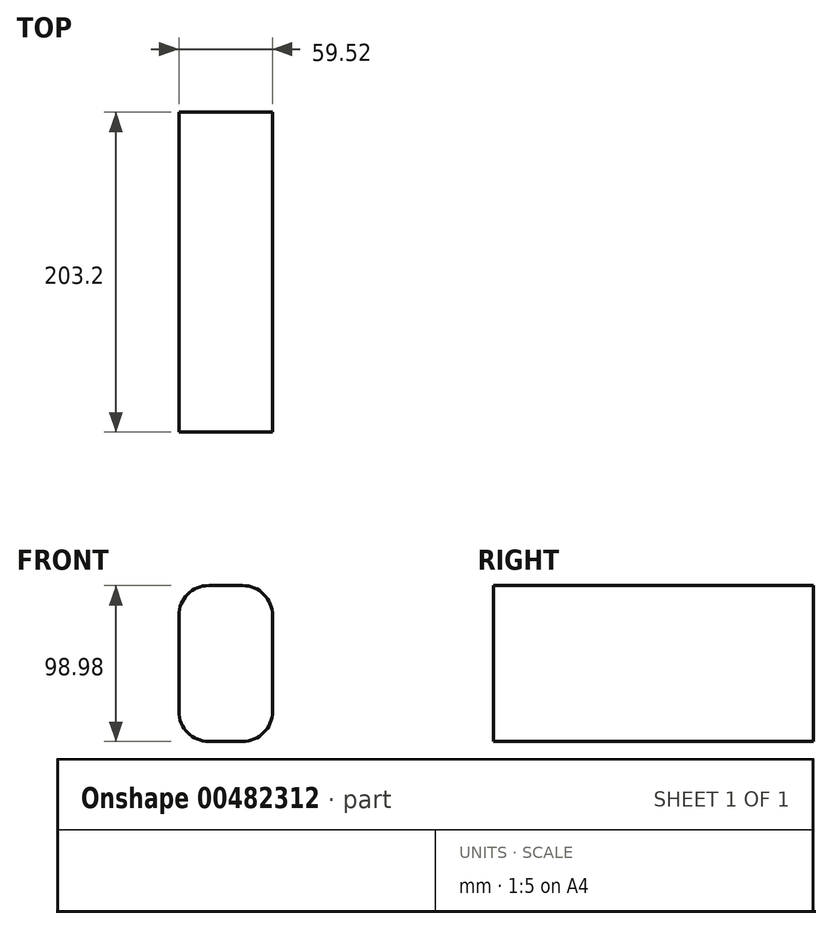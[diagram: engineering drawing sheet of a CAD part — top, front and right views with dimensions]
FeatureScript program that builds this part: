
annotation { "Feature Type Name" : "Feature", "Feature Type Description" : "" }
export const myFeature = defineFeature(function(context is Context, id is Id, definition is map)
    precondition{}
    {
        {
            var Q0;
            Q0=qCreatedBy(makeId("Front.planeOp"),FACE);
            var sketch = newSketch(context, id + "F0", { "sketchPlane" : qUnion([Q0])});
            skLineSegment(sketch, "E0.bottom", {"start": v(0, 46.05) * mm, "end": v(59.52, 46.05) * mm});
            skLineSegment(sketch, "E0.top", {"start": v(0, -52.93) * mm, "end": v(59.52, -52.93) * mm});
            skLineSegment(sketch, "E0.left", {"start": v(0, 46.05) * mm, "end": v(0, -52.93) * mm});
            skLineSegment(sketch, "E0.right", {"start": v(59.52, 46.05) * mm, "end": v(59.52, -52.93) * mm});
            skSolve(sketch);
        }
        {
            var Q0;
            Q0=makeQuery(id+"F0.imprint","IMPRINT",FACE,{"disambiguationData":[TD([[makeQuery(id+"F0.imprint","IMPRINT",EDGE,{"derivedFrom":sQuery(id+"F0.wireOp",EDGE,"E0.bottom")}),-1.0]])]});
            extrude(context, id + "F1", {"entities" : qUnion([Q0]), "depth" : 203.2 * mm, "offsetDistance" : 25.4 * mm});
        }
        {
            var Q0;
            Q0=makeQuery(id+"F1.opExtrude","SWEPT_EDGE",EDGE,{"disambiguationData":[OSD([sQuery(id+"F0.wireOp",EDGE,"E0.top"),sQuery(id+"F0.wireOp",EDGE,"E0.left")])]});
            var Q1;
            Q1=makeQuery(id+"F1.opExtrude","SWEPT_EDGE",EDGE,{"disambiguationData":[OSD([sQuery(id+"F0.wireOp",EDGE,"E0.top"),sQuery(id+"F0.wireOp",EDGE,"E0.right")])]});
            var Q2;
            Q2=makeQuery(id+"F1.opExtrude","SWEPT_EDGE",EDGE,{"disambiguationData":[OSD([sQuery(id+"F0.wireOp",EDGE,"E0.bottom"),sQuery(id+"F0.wireOp",EDGE,"E0.left")])]});
            var Q3;
            Q3=makeQuery(id+"F1.opExtrude","SWEPT_EDGE",EDGE,{"disambiguationData":[OSD([sQuery(id+"F0.wireOp",EDGE,"E0.bottom"),sQuery(id+"F0.wireOp",EDGE,"E0.right")])]});
            fillet(context, id + "F2", {"entities" : qUnion([Q0, Q1, Q2, Q3]), "radius" : 19.05 * mm, "tangentPropagation" : true, "allowEdgeOverflow" : false});
        }
    });
